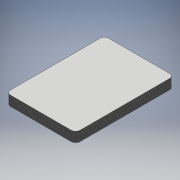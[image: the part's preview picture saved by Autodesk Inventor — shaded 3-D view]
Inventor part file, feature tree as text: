
AUTODESK INVENTOR PART (.ipt)
format: ipt  version: 2018 (Build 220112000, 112)  size: 282,624 bytes
history: native  units: mm
features: extrude x1, pattern_linear x1, sketch x1
ambient origin geometry x8: Origin, YZ Plane, XZ Plane, XY Plane, X Axis, Y Axis, Z Axis, Center Point
bodies: Solid1 (feature_tree)
feature tree (3):
  extrude  "Extrusion1"  Depth=89.0mm
  pattern_linear  "Rectangular Pattern1"  Spacing1=4.0mm  [1 undecoded]
  sketch  "Sketch1"  dims[d0=63.0mm d1=89.0mm d2=4.0mm d3=0.27mm d4=0.0mm d5=310.0mm d7=8.73mm]
note: 1 required parameter value undecoded (feature->parameter linkage not recoverable at this tier; creation-order binding heuristic only, values carry confidence <= 0.55)
